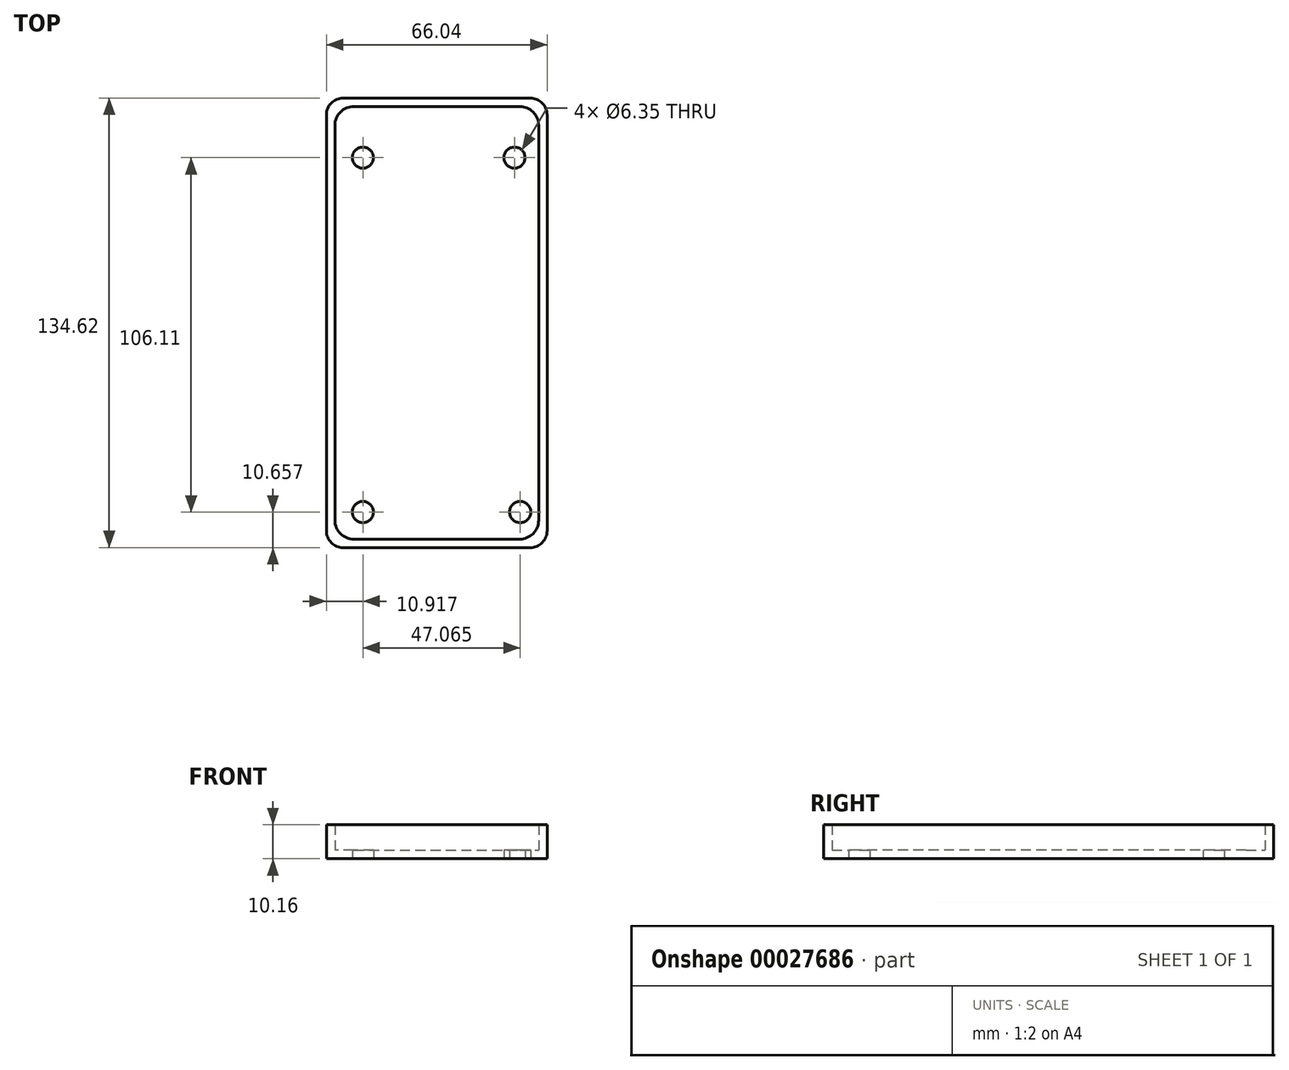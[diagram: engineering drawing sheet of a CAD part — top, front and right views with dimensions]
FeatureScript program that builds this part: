
annotation { "Feature Type Name" : "Feature", "Feature Type Description" : "" }
export const myFeature = defineFeature(function(context is Context, id is Id, definition is map)
    precondition{}
    {
        {
            var Q0;
            Q0=qCreatedBy(makeId("Top.planeOp"),FACE);
            var sketch = newSketch(context, id + "F0", { "sketchPlane" : qUnion([Q0])});
            skLineSegment(sketch, "E0.bottom", {"start": v(-50.28, 63.92) * mm, "end": v(15.76, 63.92) * mm});
            skLineSegment(sketch, "E0.top", {"start": v(-50.28, -70.7) * mm, "end": v(15.76, -70.7) * mm});
            skLineSegment(sketch, "E0.left", {"start": v(-50.28, 63.92) * mm, "end": v(-50.28, -70.7) * mm});
            skLineSegment(sketch, "E0.right", {"start": v(15.76, 63.92) * mm, "end": v(15.76, -70.7) * mm});
            skSolve(sketch);
        }
        {
            var Q0;
            Q0=makeQuery(id+"F0.imprint","IMPRINT",FACE,{"disambiguationData":[TD([[makeQuery(id+"F0.imprint","IMPRINT",EDGE,{"derivedFrom":sQuery(id+"F0.wireOp",EDGE,"E0.bottom")}),-1.0]])]});
            extrude(context, id + "F1", {"entities" : qUnion([Q0]), "depth" : 10.16 * mm});
        }
        {
            var Q0;
            Q0=makeQuery(id+"F1.opExtrude","CAP_FACE",FACE,{"disambiguationData":[OSD([sQuery(id+"F0.wireOp",EDGE,"E0.bottom"),sQuery(id+"F0.wireOp",EDGE,"E0.top"),sQuery(id+"F0.wireOp",EDGE,"E0.left"),sQuery(id+"F0.wireOp",EDGE,"E0.right")])],"isStart":false});
            shell(context, id + "F2", {"entities" : qUnion([Q0]), "thickness" : 2.54 * mm});
        }
        {
            var Q0;
            Q0=makeQuery(id+"F1.opExtrude","SWEPT_EDGE",EDGE,{"disambiguationData":[OSD([sQuery(id+"F0.wireOp",EDGE,"E0.bottom"),sQuery(id+"F0.wireOp",EDGE,"E0.left")])]});
            var Q1;
            Q1=makeQuery(id+"F1.opExtrude","SWEPT_EDGE",EDGE,{"disambiguationData":[OSD([sQuery(id+"F0.wireOp",EDGE,"E0.bottom"),sQuery(id+"F0.wireOp",EDGE,"E0.right")])]});
            var Q2;
            Q2=makeQuery(id+"F1.opExtrude","SWEPT_EDGE",EDGE,{"disambiguationData":[OSD([sQuery(id+"F0.wireOp",EDGE,"E0.top"),sQuery(id+"F0.wireOp",EDGE,"E0.right")])]});
            var Q3;
            Q3=makeQuery(id+"F1.opExtrude","SWEPT_EDGE",EDGE,{"disambiguationData":[OSD([sQuery(id+"F0.wireOp",EDGE,"E0.top"),sQuery(id+"F0.wireOp",EDGE,"E0.left")])]});
            fillet(context, id + "F3", {"entities" : qUnion([Q0, Q1, Q2, Q3]), "radius" : 5.08 * mm, "tangentPropagation" : true, "allowEdgeOverflow" : false});
        }
        {
            var Q0;
            Q0=makeQuery(id+"F2.opShell","OFFSET_EDGE",EDGE,{"disambiguationData":[OSD([sQuery(id+"F0.wireOp",EDGE,"E0.bottom"),sQuery(id+"F0.wireOp",EDGE,"E0.left")])]});
            var Q1;
            Q1=makeQuery(id+"F2.opShell","OFFSET_EDGE",EDGE,{"disambiguationData":[OSD([sQuery(id+"F0.wireOp",EDGE,"E0.bottom"),sQuery(id+"F0.wireOp",EDGE,"E0.right")])]});
            var Q2;
            Q2=makeQuery(id+"F2.opShell","OFFSET_EDGE",EDGE,{"disambiguationData":[OSD([sQuery(id+"F0.wireOp",EDGE,"E0.top"),sQuery(id+"F0.wireOp",EDGE,"E0.left")])]});
            var Q3;
            Q3=makeQuery(id+"F2.opShell","OFFSET_EDGE",EDGE,{"disambiguationData":[OSD([sQuery(id+"F0.wireOp",EDGE,"E0.top"),sQuery(id+"F0.wireOp",EDGE,"E0.right")])]});
            fillet(context, id + "F4", {"entities" : qUnion([Q0, Q1, Q2, Q3]), "radius" : 5.65 * mm, "tangentPropagation" : true, "allowEdgeOverflow" : false});
        }
        {
            var Q0;
            Q0=qCreatedBy(makeId("Top.planeOp"),FACE);
            var sketch = newSketch(context, id + "F5", { "sketchPlane" : qUnion([Q0])});
            skPoint(sketch, "E1", {"position": v(-39.36, 46.07) * mm});
            skPoint(sketch, "E2", {"position": v(6, 46.07) * mm});
            skPoint(sketch, "E3", {"position": v(-39.36, -60.04) * mm});
            skPoint(sketch, "E4", {"position": v(7.7, -60.04) * mm});
            skSolve(sketch);
        }
        {
            var Q0;
            Q0=sQuery(id+"F5.wireOp",VERTEX,"E1");
            var Q1;
            Q1=sQuery(id+"F5.wireOp",VERTEX,"E2");
            var Q2;
            Q2=sQuery(id+"F5.wireOp",VERTEX,"E4");
            var Q3;
            Q3=sQuery(id+"F5.wireOp",VERTEX,"E3");
            var Q4;
            Q4=makeQuery(id+"F1.opExtrude","SWEPT_BODY",BODY,{"disambiguationData":[OSD([sQuery(id+"F0.wireOp",EDGE,"E0.bottom"),sQuery(id+"F0.wireOp",EDGE,"E0.top"),sQuery(id+"F0.wireOp",EDGE,"E0.left"),sQuery(id+"F0.wireOp",EDGE,"E0.right")])]});
            hole(context, id + "F6", {"style" : HoleStyle.SIMPLE, "holeDiameter" : 6.35 * mm, "endStyle" : HoleEndStyle.THROUGH, "oppositeDirection" : true, "locations" : qUnion([Q0, Q1, Q2, Q3]), "scope" : qUnion([Q4])});
        }
    });
